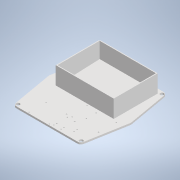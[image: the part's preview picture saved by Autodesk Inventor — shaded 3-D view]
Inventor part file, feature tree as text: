
AUTODESK INVENTOR PART (.ipt)
format: ipt  version: 2021 (Build 250183000, 183)  size: 230,400 bytes
history: native  units: mm
features: reference x9, extrude x7, sketch x7, other x3, projected_geometry x2
ambient origin geometry x8: Origin, YZ Plane, XZ Plane, XY Plane, X Axis, Y Axis, Z Axis, Center Point
bodies: Solid1 (feature_tree)
feature tree (28):
  extrude  "Extrusion1"  TaperAngle=0.0deg  [1 undecoded]
  extrude  "Extrusion2"  Depth=95.0mm
  extrude  "Extrusion3"  Depth=95.0mm
  extrude  "Extrusion4"  Depth=2.5mm
  extrude  "Extrusion6"  Depth=2.5mm
  extrude  "Extrusion7"  Depth=50.0mm TaperAngle=0.0deg
  extrude  "Extrusion8"  Depth=10.0mm TaperAngle=0.0deg
  sketch  "Sketch1"  dims[d0=5.0mm d1=0.0mm d2=0.0mm d3=0.0mm]
  reference  "Reference1"
  sketch  "Sketch2"  dims[d4=50.0mm d5=0.0mm d6=95.0mm]
  reference  "Reference2"
  reference  "Reference3"
  reference  "Reference4"
  reference  "Reference5"
  sketch  "Sketch3"  dims[d7=120.0mm d8=95.0mm]
  reference  "Reference6"
  reference  "Reference7"
  reference  "Reference8"
  reference  "Reference9"
  sketch  "Sketch4"  dims[d9=120.0mm d10=2.5mm]
  sketch  "Sketch6"  dims[d11=2.5mm d12=2.5mm]
  projected_geometry  "Projected Loop1"
  sketch  "Sketch7"  dims[d13=2.5mm d14=50.0mm d15=0.0mm]
  sketch  "Sketch8"  dims[d26=5.0mm d27=10.0mm d28=0.0mm d29=10.0mm d30=0.0mm d31=57.666667mm d33=57.667mm d34=5.0mm d35=5.0mm d36=5.0mm d37=5.0mm d38=2.5mm d39=2.5mm d40=2.5mm d41=2.5mm d42=10.0mm d43=0.0mm]
  projected_geometry  "Projected Loop2"
  parser-record x1  (decoder bookkeeping rows leaked as tree rows — omitted from the tree; the rows remain in map.json)
  other  "ilmbt_3d_v1.iam"
  other  "base_:1"
note: 1 required parameter value undecoded (feature->parameter linkage not recoverable at this tier; creation-order binding heuristic only, values carry confidence <= 0.55)
note: 1 file-system path scrubbed to <path> (originals preserved in map.json)
